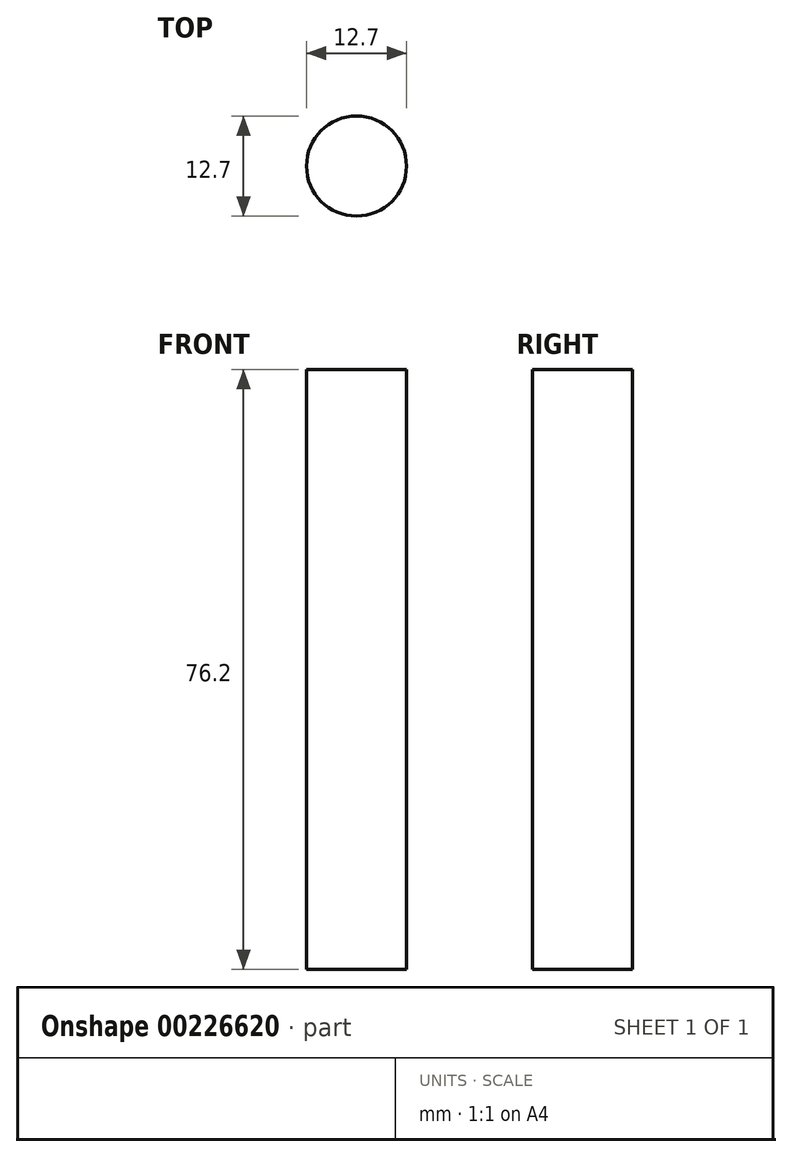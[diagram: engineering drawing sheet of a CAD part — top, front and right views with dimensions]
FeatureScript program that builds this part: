
annotation { "Feature Type Name" : "Feature", "Feature Type Description" : "" }
export const myFeature = defineFeature(function(context is Context, id is Id, definition is map)
    precondition{}
    {
        {
            var Q0;
            Q0=qCreatedBy(makeId("Top.planeOp"),FACE);
            var sketch = newSketch(context, id + "F0", { "sketchPlane" : qUnion([Q0])});
            skCircle(sketch, "E0", {"center": v(0, 0) * mm, "radius": 6.35 * mm});
            skSolve(sketch);
        }
        {
            var Q0;
            Q0=makeQuery(id+"F0.imprint","IMPRINT",FACE,{"disambiguationData":[TD([[makeQuery(id+"F0.imprint","IMPRINT",EDGE,{"derivedFrom":sQuery(id+"F0.wireOp",EDGE,"E0")}),1.0]])]});
            extrude(context, id + "F1", {"entities" : qUnion([Q0]), "depth" : 76.2 * mm});
        }
    });
